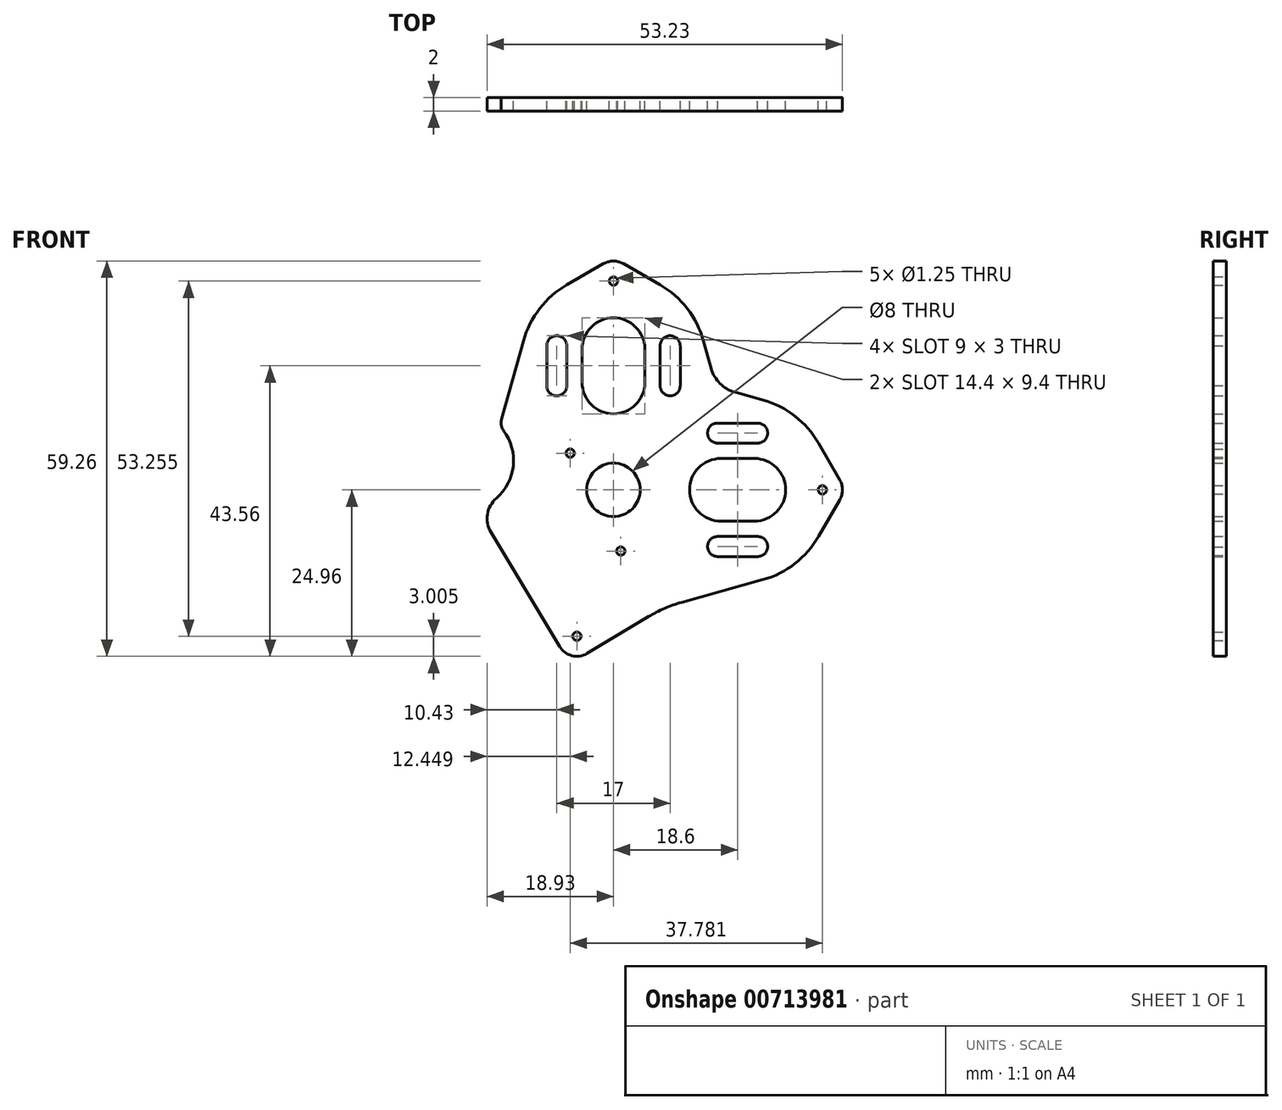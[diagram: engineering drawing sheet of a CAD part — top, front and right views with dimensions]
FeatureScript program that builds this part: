
annotation { "Feature Type Name" : "Feature", "Feature Type Description" : "" }
export const myFeature = defineFeature(function(context is Context, id is Id, definition is map)
    precondition{}
    {
        {
            var Q0;
            Q0=qCreatedBy(makeId("Front.planeOp"),FACE);
            var sketch = newSketch(context, id + "F0", { "sketchPlane" : qUnion([Q0])});
            skCircle(sketch, "E0", {"center": v(0, 0) * mm, "radius": 4 * mm});
            skLineSegment(sketch, "E1", {"start": v(-18.36, -6.34) * mm, "end": v(-8.05, -23.5) * mm});
            skLineSegment(sketch, "E2", {"start": v(-3.93, -24.53) * mm, "end": v(5.26, -19) * mm});
            skCircle(sketch, "E3", {"center": v(0, 0) * mm, "radius": 9.25 * mm, "construction": true});
            skCircle(sketch, "E4", {"center": v(1.1, -9.18) * mm, "radius": 0.62 * mm});
            skCircle(sketch, "E5", {"center": v(0, 0) * mm, "radius": 8.5 * mm, "construction": true});
            skCircle(sketch, "E6", {"center": v(-6.48, 5.5) * mm, "radius": 0.62 * mm});
            skArc(sketch, "E7", {"start": v(-4.7, 16.1) * mm, "mid": v(0, 11.4) * mm, "end": v(4.7, 16.1) * mm});
            skLineSegment(sketch, "E8", {"start": v(0, 0) * mm, "end": v(0, 43.43) * mm, "construction": true});
            skLineSegment(sketch, "E9", {"start": v(4.7, 16.1) * mm, "end": v(4.7, 21.1) * mm});
            skLineSegment(sketch, "E10", {"start": v(-4.7, 16.1) * mm, "end": v(-4.7, 21.1) * mm});
            skArc(sketch, "E11.trimOffspring", {"start": v(4.7, 21.1) * mm, "mid": v(0, 25.8) * mm, "end": v(-4.7, 21.1) * mm});
            skArc(sketch, "E12", {"start": v(13.48, 22.36) * mm, "mid": v(11.06, 27.18) * mm, "end": v(7, 30.73) * mm});
            skLineSegment(sketch, "E13", {"start": v(13.48, 22.36) * mm, "end": v(14.66, 18.14) * mm});
            skLineSegment(sketch, "E14.MirrorCS", {"start": v(-13.48, 22.36) * mm, "end": v(-16.77, 10.6) * mm});
            skArc(sketch, "E15", {"start": v(-17.55, -1.26) * mm, "mid": v(-15.02, 3.58) * mm, "end": v(-16.45, 8.86) * mm});
            skArc(sketch, "E16.filletArc", {"start": v(-17.55, -1.26) * mm, "mid": v(-18.88, -3.66) * mm, "end": v(-18.36, -6.34) * mm});
            skLineSegment(sketch, "E17", {"start": v(-17.05, 9.58) * mm, "end": v(-22.26, -9.08) * mm, "construction": true});
            skLineSegment(sketch, "E18", {"start": v(-18.36, -6.34) * mm, "end": v(-20.5, -2.77) * mm, "construction": true});
            skPoint(sketch, "E19.visualSharp", {"position": v(-17.05, 9.58) * mm});
            skArc(sketch, "E19.filletArc", {"start": v(-16.77, 10.6) * mm, "mid": v(-16.81, 9.7) * mm, "end": v(-16.45, 8.86) * mm});
            skCircle(sketch, "E20", {"center": v(-5.47, -21.96) * mm, "radius": 0.62 * mm});
            skPoint(sketch, "E21.visualSharp", {"position": v(-6.5, -26.07) * mm});
            skArc(sketch, "E21.filletArc", {"start": v(-8.05, -23.5) * mm, "mid": v(-6.2, -24.87) * mm, "end": v(-3.93, -24.53) * mm});
            skLineSegment(sketch, "E22", {"start": v(-8.29, 18.6) * mm, "end": v(14.54, 18.6) * mm, "construction": true});
            skArc(sketch, "E23", {"start": v(7, 15.6) * mm, "mid": v(8.5, 14.1) * mm, "end": v(10, 15.62) * mm});
            skLineSegment(sketch, "E24", {"start": v(7, 15.6) * mm, "end": v(7, 18.6) * mm});
            skLineSegment(sketch, "E25", {"start": v(10, 15.58) * mm, "end": v(10, 18.6) * mm});
            skLineSegment(sketch, "E26.MirrorCS", {"start": v(10, 21.62) * mm, "end": v(10, 18.6) * mm});
            skLineSegment(sketch, "E27.MirrorCS", {"start": v(7, 21.6) * mm, "end": v(7, 18.6) * mm});
            skArc(sketch, "E28.MirrorCS", {"start": v(7, 21.6) * mm, "mid": v(8.5, 23.1) * mm, "end": v(10, 21.58) * mm});
            skArc(sketch, "E29.MirrorCS", {"start": v(-7, 21.6) * mm, "mid": v(-8.5, 23.1) * mm, "end": v(-10, 21.58) * mm});
            skArc(sketch, "E30.MirrorCS", {"start": v(-7, 15.6) * mm, "mid": v(-8.5, 14.1) * mm, "end": v(-10, 15.62) * mm});
            skLineSegment(sketch, "E31.MirrorCS", {"start": v(-7, 15.6) * mm, "end": v(-7, 18.6) * mm});
            skLineSegment(sketch, "E32.MirrorCS", {"start": v(-10, 15.58) * mm, "end": v(-10, 18.6) * mm});
            skLineSegment(sketch, "E33.MirrorCS", {"start": v(-10, 21.62) * mm, "end": v(-10, 18.6) * mm});
            skLineSegment(sketch, "E34.MirrorCS", {"start": v(-7, 21.6) * mm, "end": v(-7, 18.6) * mm});
            skCircle(sketch, "E35", {"center": v(0, 31.3) * mm, "radius": 0.62 * mm});
            skArc(sketch, "E36", {"start": v(1.5, 33.9) * mm, "mid": v(0, 34.3) * mm, "end": v(-1.5, 33.9) * mm});
            skArc(sketch, "E37.trimOffspring", {"start": v(-7, 30.73) * mm, "mid": v(-11.06, 27.18) * mm, "end": v(-13.48, 22.36) * mm});
            skLineSegment(sketch, "E38", {"start": v(0, 0) * mm, "end": v(-16.29, -9.79) * mm, "construction": true});
            skLineSegment(sketch, "E39", {"start": v(-1.5, 33.9) * mm, "end": v(-7, 30.73) * mm});
            skLineSegment(sketch, "E40", {"start": v(1.5, 33.9) * mm, "end": v(7, 30.73) * mm});
            skLineSegment(sketch, "E41", {"start": v(0, 0) * mm, "end": v(-6.48, 5.5) * mm, "construction": true});
            skLineSegment(sketch, "E42", {"start": v(0, 0) * mm, "end": v(32.74, 32.74) * mm, "construction": true});
            skArc(sketch, "E43.MirrorCS", {"start": v(22.36, 13.48) * mm, "mid": v(27.18, 11.06) * mm, "end": v(30.73, 7) * mm});
            skLineSegment(sketch, "E44.MirrorCS", {"start": v(33.9, 1.5) * mm, "end": v(30.73, 7) * mm});
            skArc(sketch, "E45.MirrorCS", {"start": v(33.9, 1.5) * mm, "mid": v(34.3, 0) * mm, "end": v(33.9, -1.5) * mm});
            skLineSegment(sketch, "E46.MirrorCS", {"start": v(33.9, -1.5) * mm, "end": v(30.73, -7) * mm});
            skArc(sketch, "E47.MirrorCS", {"start": v(30.73, -7) * mm, "mid": v(27.18, -11.06) * mm, "end": v(22.36, -13.48) * mm});
            skLineSegment(sketch, "E48.MirrorCS", {"start": v(21.62, 10) * mm, "end": v(18.6, 10) * mm});
            skLineSegment(sketch, "E49.MirrorCS", {"start": v(21.6, 7) * mm, "end": v(18.6, 7) * mm});
            skArc(sketch, "E50.MirrorCS", {"start": v(21.6, 7) * mm, "mid": v(23.1, 8.5) * mm, "end": v(21.58, 10) * mm});
            skLineSegment(sketch, "E51.MirrorCS", {"start": v(15.6, 7) * mm, "end": v(18.6, 7) * mm});
            skLineSegment(sketch, "E52.MirrorCS", {"start": v(15.58, 10) * mm, "end": v(18.6, 10) * mm});
            skArc(sketch, "E53.MirrorCS", {"start": v(15.6, 7) * mm, "mid": v(14.1, 8.5) * mm, "end": v(15.62, 10) * mm});
            skLineSegment(sketch, "E54.MirrorCS", {"start": v(16.1, 4.7) * mm, "end": v(21.1, 4.7) * mm});
            skArc(sketch, "E55.MirrorCS", {"start": v(21.1, 4.7) * mm, "mid": v(25.8, 0) * mm, "end": v(21.1, -4.7) * mm});
            skLineSegment(sketch, "E56.MirrorCS", {"start": v(16.1, -4.7) * mm, "end": v(21.1, -4.7) * mm});
            skArc(sketch, "E57.MirrorCS", {"start": v(16.1, -4.7) * mm, "mid": v(11.4, 0) * mm, "end": v(16.1, 4.7) * mm});
            skLineSegment(sketch, "E58.MirrorCS", {"start": v(21.6, -7) * mm, "end": v(18.6, -7) * mm});
            skArc(sketch, "E59.MirrorCS", {"start": v(21.6, -7) * mm, "mid": v(23.1, -8.5) * mm, "end": v(21.58, -10) * mm});
            skLineSegment(sketch, "E60.MirrorCS", {"start": v(21.62, -10) * mm, "end": v(18.6, -10) * mm});
            skLineSegment(sketch, "E61.MirrorCS", {"start": v(15.58, -10) * mm, "end": v(18.6, -10) * mm});
            skArc(sketch, "E62.MirrorCS", {"start": v(15.6, -7) * mm, "mid": v(14.1, -8.5) * mm, "end": v(15.62, -10) * mm});
            skLineSegment(sketch, "E63.MirrorCS", {"start": v(15.6, -7) * mm, "end": v(18.6, -7) * mm});
            skCircle(sketch, "E64.MirrorC", {"center": v(31.3, 0) * mm, "radius": 0.62 * mm});
            skLineSegment(sketch, "E65.MirrorCS", {"start": v(22.36, 13.48) * mm, "end": v(18.14, 14.66) * mm});
            skLineSegment(sketch, "E66", {"start": v(22.36, -13.48) * mm, "end": v(10.19, -16.88) * mm});
            skPoint(sketch, "E67.visualSharp", {"position": v(15.42, 15.42) * mm});
            skArc(sketch, "E67.filletArc", {"start": v(14.66, 18.14) * mm, "mid": v(15.94, 15.94) * mm, "end": v(18.14, 14.66) * mm});
            skPoint(sketch, "E68.visualSharp", {"position": v(7.58, -17.6) * mm});
            skArc(sketch, "E68.filletArc", {"start": v(10.19, -16.88) * mm, "mid": v(7.65, -17.78) * mm, "end": v(5.26, -19) * mm});
            skSolve(sketch);
        }
        {
            var Q0;
            Q0=makeQuery(id+"F0.imprint","IMPRINT",FACE,{"disambiguationData":[TD([[makeQuery(id+"F0.imprint","IMPRINT",EDGE,{"derivedFrom":sQuery(id+"F0.wireOp",EDGE,"E0")}),-1.0]])]});
            extrude(context, id + "F1", {"entities" : qUnion([Q0]), "depth" : 2 * mm, "offsetDistance" : 25 * mm});
        }
    });
